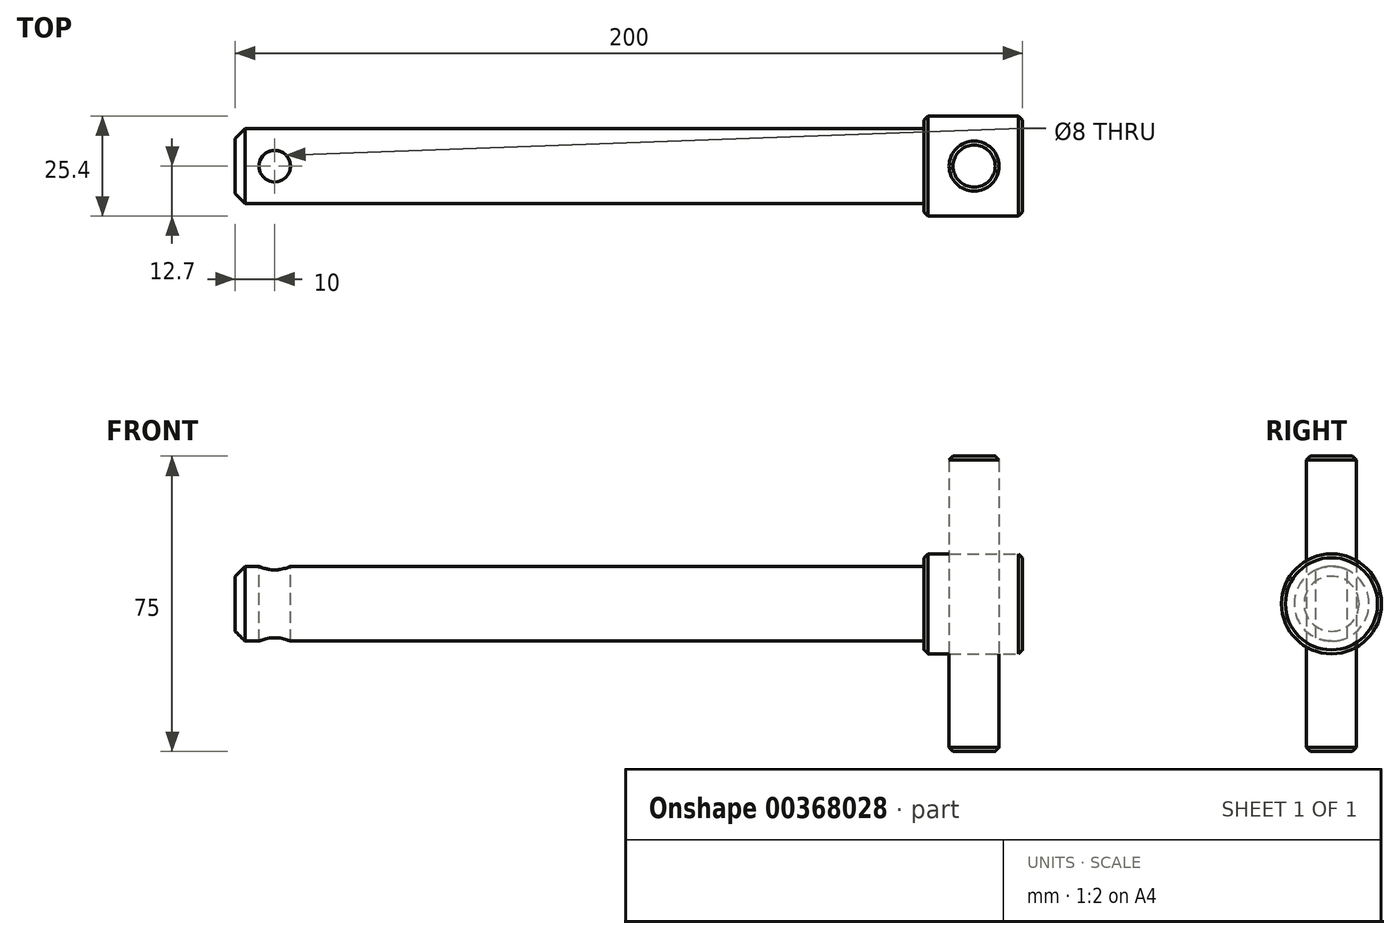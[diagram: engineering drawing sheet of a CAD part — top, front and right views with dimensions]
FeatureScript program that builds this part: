
annotation { "Feature Type Name" : "Feature", "Feature Type Description" : "" }
export const myFeature = defineFeature(function(context is Context, id is Id, definition is map)
    precondition{}
    {
        {
            var Q0;
            Q0=qCreatedBy(makeId("Right.planeOp"),FACE);
            var sketch = newSketch(context, id + "F0", { "sketchPlane" : qUnion([Q0])});
            skCircle(sketch, "E0", {"center": v(0, 0) * mm, "radius": 9.5 * mm});
            skSolve(sketch);
        }
        {
            var Q0;
            Q0=makeQuery(id+"F0.imprint","IMPRINT",FACE,{"disambiguationData":[TD([[makeQuery(id+"F0.imprint","IMPRINT",EDGE,{"derivedFrom":sQuery(id+"F0.wireOp",EDGE,"E0")}),1.0]])]});
            extrude(context, id + "F1", {"entities" : qUnion([Q0]), "endBound" : BoundingType.SYMMETRIC, "depth" : 200 * mm});
        }
        {
            var Q0;
            Q0=makeQuery(id+"F1.opExtrude","CAP_FACE",FACE,{"disambiguationData":[OSD([sQuery(id+"F0.wireOp",EDGE,"E0")])],"isStart":false});
            var sketch = newSketch(context, id + "F2", { "sketchPlane" : qUnion([Q0])});
            skCircle(sketch, "E1", {"center": v(0, 0) * mm, "radius": 12.7 * mm});
            skSolve(sketch);
        }
        {
            var Q0;
            Q0=makeQuery(id+"F2.imprint","IMPRINT",FACE,{"disambiguationData":[TD([[makeQuery(id+"F2.imprint","IMPRINT",EDGE,{"derivedFrom":sQuery(id+"F2.wireOp",EDGE,"E1")}),1.0]])]});
            extrude(context, id + "F3", {"entities" : qUnion([Q0]), "operationType" : NewBodyOperationType.ADD, "oppositeDirection" : true, "depth" : 25 * mm});
        }
        {
            var Q0;
            Q0=qCreatedBy(makeId("Top.planeOp"),FACE);
            var sketch = newSketch(context, id + "F4", { "sketchPlane" : qUnion([Q0])});
            skCircle(sketch, "E2", {"center": v(-90, 0) * mm, "radius": 4 * mm});
            skCircle(sketch, "E3", {"center": v(87.7, 0) * mm, "radius": 6.35 * mm});
            skSolve(sketch);
        }
        {
            var Q0;
            Q0=makeQuery(id+"F4.imprint","IMPRINT",FACE,{"disambiguationData":[TD([[makeQuery(id+"F4.imprint","IMPRINT",EDGE,{"derivedFrom":sQuery(id+"F4.wireOp",EDGE,"E3")}),1.0]])]});
            extrude(context, id + "F5", {"entities" : qUnion([Q0]), "endBound" : BoundingType.SYMMETRIC, "depth" : 75 * mm});
        }
        {
            var Q0;
            Q0=makeQuery(id+"F4.imprint","IMPRINT",FACE,{"disambiguationData":[TD([[makeQuery(id+"F4.imprint","IMPRINT",EDGE,{"derivedFrom":sQuery(id+"F4.wireOp",EDGE,"E2")}),1.0]])]});
            extrude(context, id + "F6", {"entities" : qUnion([Q0]), "operationType" : NewBodyOperationType.REMOVE, "endBound" : BoundingType.SYMMETRIC, "oppositeDirection" : true, "depth" : 25 * mm});
        }
        {
            var Q0;
            Q0=makeQuery(id+"F1.opExtrude","CAP_FACE",FACE,{"disambiguationData":[OSD([sQuery(id+"F0.wireOp",EDGE,"E0")])],"isStart":true});
            chamfer(context, id + "F7", {"entities" : qUnion([Q0]), "width" : 2.5 * mm, "tangentPropagation" : true});
        }
        {
            var Q0;
            Q0=makeQuery(id+"F3.opExtrude","CAP_EDGE",EDGE,{"disambiguationData":[OSD([sQuery(id+"F2.wireOp",EDGE,"E1")])],"isStart":false});
            var Q1;
            Q1=makeQuery(id+"F3.opExtrude","CAP_EDGE",EDGE,{"disambiguationData":[OSD([sQuery(id+"F2.wireOp",EDGE,"E1")])],"isStart":true});
            var Q2;
            Q2=makeQuery(id+"F5.opExtrude","CAP_FACE",FACE,{"disambiguationData":[OSD([sQuery(id+"F4.wireOp",EDGE,"E3")])],"isStart":true});
            var Q3;
            Q3=makeQuery(id+"F5.opExtrude","CAP_FACE",FACE,{"disambiguationData":[OSD([sQuery(id+"F4.wireOp",EDGE,"E3")])],"isStart":false});
            chamfer(context, id + "F8", {"entities" : qUnion([Q0, Q1, Q2, Q3]), "width" : 1 * mm, "tangentPropagation" : true});
        }
    });
